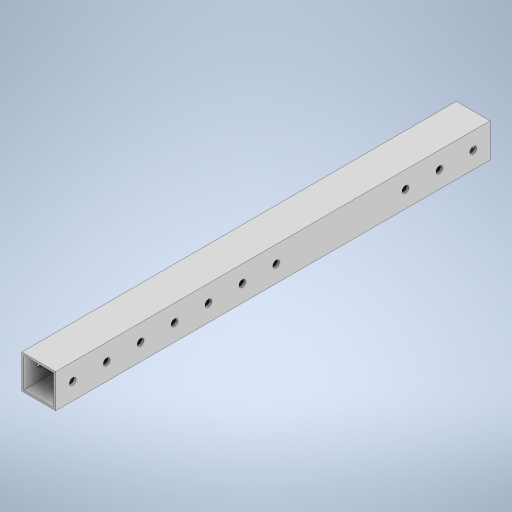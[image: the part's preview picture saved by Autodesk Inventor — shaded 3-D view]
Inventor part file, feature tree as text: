
AUTODESK INVENTOR PART (.ipt)
format: ipt  version: 2024 (Build 280153000, 153)  size: 418,816 bytes
history: native  units: in
note: dims shown in document units (in); Inventor stores cm internally (conversion verified against a paired STEP export)
features: extrude x14, sketch x14, projected_geometry x6
ambient origin geometry x8: Origin, YZ Plane, XZ Plane, XY Plane, X Axis, Y Axis, Z Axis, Center Point
bodies: Solid1 (feature_tree)
feature tree (34):
  extrude  "Extrusion1"  Depth=1.0in
  extrude  "Extrusion2"  Depth=0.0625in TaperAngle=0.0deg
  extrude  "Extrusion4"  Depth=0.5in
  extrude  "Extrusion5"  Depth=1.0in
  extrude  "Extrusion6"  Depth=8.811in
  extrude  "Extrusion7"  Depth=0.5in
  extrude  "Extrusion8"  Depth=1.0in
  extrude  "Extrusion9"  Depth=1.0in
  extrude  "Extrusion10"  Depth=2.0in TaperAngle=0.0deg
  extrude  "Extrusion11"  Depth=1.0in
  sketch  "Sketch13"  dims[d29=1.0in d30=0.203in]
  extrude  "Extrusion12"  Depth=1.0in
  extrude  "Extrusion13"  Depth=0.5in
  extrude  "Extrusion14"  Depth=1.0in
  extrude  "Extrusion15"  Depth=1.0in
  sketch  "Sketch1"  dims[d0=1.0in d1=1.0in]
  sketch  "Sketch2"  dims[d2=0.0625in d3=24.0in d4=0.0in]
  projected_geometry  "Projected Loop1"
  sketch  "Sketch5"  dims[d5=0.203in d7=0.5in]
  sketch  "Sketch6"  dims[d8=1.0in d9=1.0in]
  sketch  "Sketch7"  dims[d10=0.0in d11=0.0in d15=8.811in]
  projected_geometry  "Projected Loop2"
  sketch  "Sketch8"  dims[d16=4.0in d17=0.0in d18=0.5in]
  sketch  "Sketch9"  dims[d19=0.203in d20=1.0in]
  projected_geometry  "Projected Loop3"
  sketch  "Sketch10"  dims[d21=0.203in d22=1.0in]
  sketch  "Sketch11"  dims[d23=0.203in d24=2.0in d25=0.0in]
  projected_geometry  "Projected Loop4"
  sketch  "Sketch12"  dims[d26=5.0in d27=0.0in d28=1.0in]
  projected_geometry  "Projected Loop5"
  sketch  "Sketch14"  dims[d31=0.203in d32=0.5in]
  projected_geometry  "Projected Loop6"
  sketch  "Sketch15"  dims[d33=1.0in d34=1.0in]
  sketch  "Sketch17"  dims[d35=0.203in d36=0.203in d37=0.203in d38=3.625in d39=0.0in d40=6.0in d41=0.0in d42=0.5in d43=1.0in d44=1.0in d45=0.203in d46=0.203in d47=0.203in d48=4.875in d49=0.0in d50=6.0in d51=0.0in d52=2.5in d53=0.0in d54=1.0in d55=1.0in d56=0.5in d57=0.0in d58=1.0in d59=0.203in d60=0.203in d61=0.203in d62=1.875in d63=0.0in d64=0.5in d65=1.875in d66=0.0in d67=0.5in d68=4.4375in d69=0.0in d13=0.5in d14=0.0344in]
